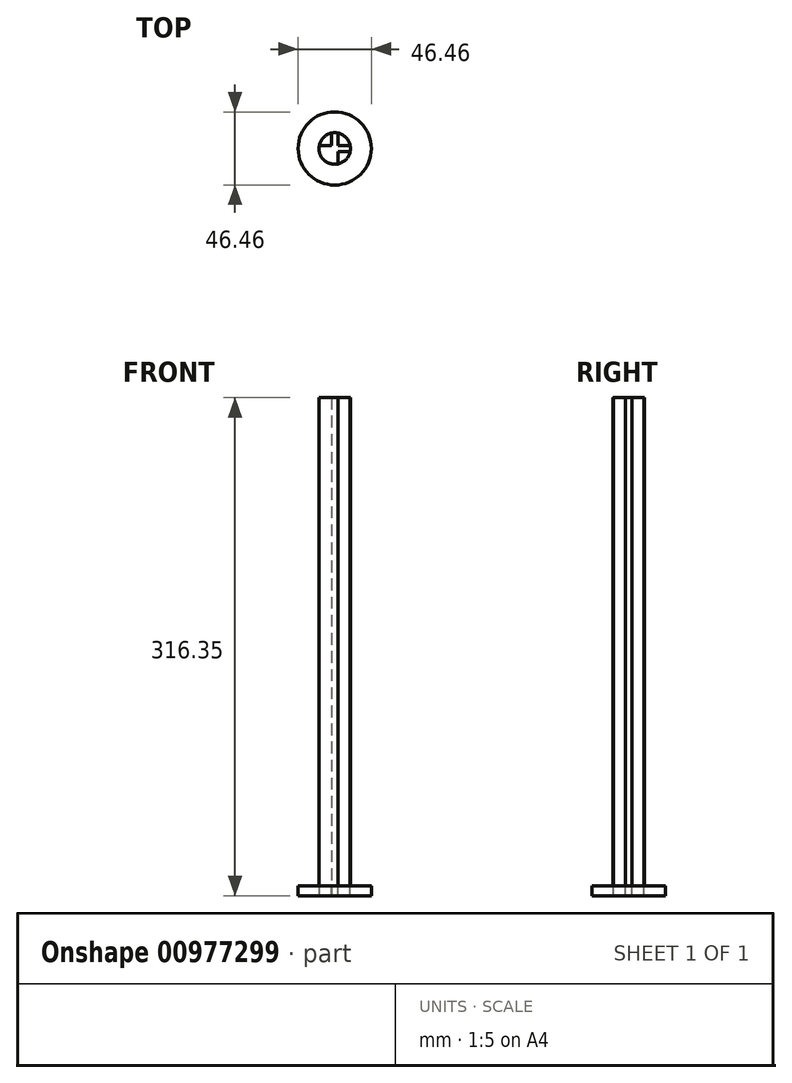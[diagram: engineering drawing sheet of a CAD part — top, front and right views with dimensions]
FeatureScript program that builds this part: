
annotation { "Feature Type Name" : "Feature", "Feature Type Description" : "" }
export const myFeature = defineFeature(function(context is Context, id is Id, definition is map)
    precondition{}
    {
        {
            var Q0;
            Q0=qCreatedBy(makeId("Top.planeOp"),FACE);
            var sketch = newSketch(context, id + "F0", { "sketchPlane" : qUnion([Q0])});
            skPoint(sketch, "E0", {"position": v(0, 0) * mm});
            skCircle(sketch, "E1", {"center": v(0, 0) * mm, "radius": 23.23 * mm});
            skPoint(sketch, "E2", {"position": v(23.64, 0) * mm});
            skLineSegment(sketch, "E3", {"start": v(17.73, 0) * mm, "end": v(23.64, 0) * mm});
            skPoint(sketch, "E4", {"position": v(20.69, 0) * mm});
            skCircle(sketch, "E5.cCircle", {"center": v(0, 0) * mm, "radius": 20.69 * mm, "construction": true});
            skLineSegment(sketch, "E5.0", {"start": v(20.69, 0) * mm, "end": v(10.34, -17.91) * mm});
            skLineSegment(sketch, "E5.1", {"start": v(10.34, -17.91) * mm, "end": v(-10.34, -17.91) * mm});
            skLineSegment(sketch, "E5.2", {"start": v(-10.34, -17.91) * mm, "end": v(-20.69, 0) * mm});
            skLineSegment(sketch, "E5.3", {"start": v(-20.69, 0) * mm, "end": v(-10.34, 17.91) * mm});
            skLineSegment(sketch, "E5.4", {"start": v(-10.34, 17.91) * mm, "end": v(10.34, 17.91) * mm});
            skLineSegment(sketch, "E5.5", {"start": v(10.34, 17.91) * mm, "end": v(20.69, 0) * mm});
            skCircle(sketch, "E6", {"center": v(0, 0) * mm, "radius": 10 * mm});
            skLineSegment(sketch, "E7.bottom", {"start": v(2, 12.5) * mm, "end": v(-2, 12.5) * mm});
            skLineSegment(sketch, "E7.top", {"start": v(2, -12.5) * mm, "end": v(-2, -12.5) * mm});
            skLineSegment(sketch, "E7.left", {"start": v(2, 12.5) * mm, "end": v(2, -12.5) * mm});
            skLineSegment(sketch, "E7.right", {"start": v(-2, 12.5) * mm, "end": v(-2, -12.5) * mm});
            skLineSegment(sketch, "E8.bottom", {"start": v(12.5, 2) * mm, "end": v(-12.5, 2) * mm});
            skLineSegment(sketch, "E8.top", {"start": v(12.5, -2) * mm, "end": v(-12.5, -2) * mm});
            skLineSegment(sketch, "E8.left", {"start": v(12.5, 2) * mm, "end": v(12.5, -2) * mm});
            skLineSegment(sketch, "E8.right", {"start": v(-12.5, 2) * mm, "end": v(-12.5, -2) * mm});
            skLineSegment(sketch, "E9.bottom", {"start": v(2, 8) * mm, "end": v(-2, 8) * mm});
            skLineSegment(sketch, "E9.top", {"start": v(2, -8) * mm, "end": v(-2, -8) * mm});
            skLineSegment(sketch, "E10", {"start": v(-8, 2) * mm, "end": v(-8, -2) * mm});
            skLineSegment(sketch, "E11", {"start": v(8, 2) * mm, "end": v(8, -2) * mm});
            skCircle(sketch, "E12", {"center": v(0, 0) * mm, "radius": 16.33 * mm});
            skSolve(sketch);
        }
        {
            var Q0;
            {var subQ0=sQuery(id+"F0.wireOp",EDGE,"E8.top");var subQ5=sQuery(id+"F0.wireOp",EDGE,"E6");var subQ7=makeQuery(id+"F0.imprint","INTERSECT",VERTEX,{"disambiguationData":[OD(0.0)],"derivedFrom":[subQ5,subQ0]});Q0=makeQuery(id+"F0.imprint","IMPRINT",FACE,{"disambiguationData":[TD([[makeQuery(id+"F0.imprint","IMPRINT",EDGE,{"disambiguationData":[TD([[subQ7,-1.0]])],"derivedFrom":subQ5}),1.0]])]});}
            var Q1;
            {var subQ0=sQuery(id+"F0.wireOp",EDGE,"E7.right");var subQ5=sQuery(id+"F0.wireOp",EDGE,"E6");var subQ6=makeQuery(id+"F0.imprint","INTERSECT",VERTEX,{"disambiguationData":[OD(0.0)],"derivedFrom":[subQ5,subQ0]});Q1=makeQuery(id+"F0.imprint","IMPRINT",FACE,{"disambiguationData":[TD([[makeQuery(id+"F0.imprint","IMPRINT",EDGE,{"disambiguationData":[TD([[subQ6,-1.0]])],"derivedFrom":subQ5}),1.0]])]});}
            var Q2;
            {var subQ0=sQuery(id+"F0.wireOp",EDGE,"E7.left");var subQ4=sQuery(id+"F0.wireOp",EDGE,"E6");var subQ5=makeQuery(id+"F0.imprint","INTERSECT",VERTEX,{"disambiguationData":[OD(0.0)],"derivedFrom":[subQ4,subQ0]});Q2=makeQuery(id+"F0.imprint","IMPRINT",FACE,{"disambiguationData":[TD([[makeQuery(id+"F0.imprint","IMPRINT",EDGE,{"disambiguationData":[TD([[subQ5,1.0]])],"derivedFrom":subQ4}),1.0]])]});}
            var Q3;
            {var subQ2=sQuery(id+"F0.wireOp",EDGE,"E6");var subQ4=sQuery(id+"F0.wireOp",EDGE,"E7.left");var subQ6=makeQuery(id+"F0.imprint","INTERSECT",VERTEX,{"disambiguationData":[OD(1.0)],"derivedFrom":[subQ2,subQ4]});Q3=makeQuery(id+"F0.imprint","IMPRINT",FACE,{"disambiguationData":[TD([[makeQuery(id+"F0.imprint","IMPRINT",EDGE,{"disambiguationData":[TD([[subQ6,-1.0]])],"derivedFrom":subQ2}),1.0]])]});}
            var Q4;
            {var subQ0=sQuery(id+"F0.wireOp",EDGE,"E9.top");Q4=makeQuery(id+"F0.imprint","IMPRINT",FACE,{"disambiguationData":[TD([[makeQuery(id+"F0.imprint","IMPRINT",EDGE,{"derivedFrom":subQ0}),-1.0]])]});}
            var Q5;
            {var subQ5=sQuery(id+"F0.wireOp",EDGE,"E11");Q5=makeQuery(id+"F0.imprint","IMPRINT",FACE,{"disambiguationData":[TD([[makeQuery(id+"F0.imprint","IMPRINT",EDGE,{"derivedFrom":subQ5}),-1.0]])]});}
            var Q6;
            {var subQ0=sQuery(id+"F0.wireOp",EDGE,"E9.bottom");Q6=makeQuery(id+"F0.imprint","IMPRINT",FACE,{"disambiguationData":[TD([[makeQuery(id+"F0.imprint","IMPRINT",EDGE,{"derivedFrom":subQ0}),1.0]])]});}
            var Q7;
            {var subQ5=sQuery(id+"F0.wireOp",EDGE,"E9.bottom");Q7=makeQuery(id+"F0.imprint","IMPRINT",FACE,{"disambiguationData":[TD([[makeQuery(id+"F0.imprint","IMPRINT",EDGE,{"derivedFrom":subQ5}),-1.0]])]});}
            var Q8;
            {var subQ5=sQuery(id+"F0.wireOp",EDGE,"E10");Q8=makeQuery(id+"F0.imprint","IMPRINT",FACE,{"disambiguationData":[TD([[makeQuery(id+"F0.imprint","IMPRINT",EDGE,{"derivedFrom":subQ5}),1.0]])]});}
            var Q9;
            {var subQ5=sQuery(id+"F0.wireOp",EDGE,"E10");Q9=makeQuery(id+"F0.imprint","IMPRINT",FACE,{"disambiguationData":[TD([[makeQuery(id+"F0.imprint","IMPRINT",EDGE,{"derivedFrom":subQ5}),-1.0]])]});}
            var Q10;
            {var subQ0=sQuery(id+"F0.wireOp",EDGE,"E8.bottom");var subQ1=sQuery(id+"F0.wireOp",EDGE,"E7.left");var subQ2=makeQuery(id+"F0.imprint","INTERSECT",VERTEX,{"derivedFrom":[subQ1,subQ0]});Q10=makeQuery(id+"F0.imprint","IMPRINT",FACE,{"disambiguationData":[TD([[makeQuery(id+"F0.imprint","IMPRINT",EDGE,{"disambiguationData":[TD([[subQ2,-1.0]])],"derivedFrom":subQ1}),-1.0]])]});}
            var Q11;
            {var subQ5=sQuery(id+"F0.wireOp",EDGE,"E9.top");Q11=makeQuery(id+"F0.imprint","IMPRINT",FACE,{"disambiguationData":[TD([[makeQuery(id+"F0.imprint","IMPRINT",EDGE,{"derivedFrom":subQ5}),1.0]])]});}
            var Q12;
            {var subQ5=sQuery(id+"F0.wireOp",EDGE,"E11");Q12=makeQuery(id+"F0.imprint","IMPRINT",FACE,{"disambiguationData":[TD([[makeQuery(id+"F0.imprint","IMPRINT",EDGE,{"derivedFrom":subQ5}),1.0]])]});}
            extrude(context, id + "F1", {"entities" : qUnion([Q0, Q1, Q2, Q3, Q4, Q5, Q6, Q7, Q8, Q9, Q10, Q11, Q12]), "depth" : 310 * mm, "offsetDistance" : 25.4 * mm});
        }
        {
            var Q0;
            {var subQ2=sQuery(id+"F0.wireOp",EDGE,"E6");var subQ4=sQuery(id+"F0.wireOp",EDGE,"E7.left");var subQ6=makeQuery(id+"F0.imprint","INTERSECT",VERTEX,{"disambiguationData":[OD(1.0)],"derivedFrom":[subQ2,subQ4]});Q0=makeQuery(id+"F0.imprint","IMPRINT",FACE,{"disambiguationData":[TD([[makeQuery(id+"F0.imprint","IMPRINT",EDGE,{"disambiguationData":[TD([[subQ6,-1.0]])],"derivedFrom":subQ2}),1.0]])]});}
            var Q1;
            {var subQ0=sQuery(id+"F0.wireOp",EDGE,"E7.left");var subQ4=sQuery(id+"F0.wireOp",EDGE,"E6");var subQ5=makeQuery(id+"F0.imprint","INTERSECT",VERTEX,{"disambiguationData":[OD(0.0)],"derivedFrom":[subQ4,subQ0]});Q1=makeQuery(id+"F0.imprint","IMPRINT",FACE,{"disambiguationData":[TD([[makeQuery(id+"F0.imprint","IMPRINT",EDGE,{"disambiguationData":[TD([[subQ5,1.0]])],"derivedFrom":subQ4}),1.0]])]});}
            var Q2;
            {var subQ5=sQuery(id+"F0.wireOp",EDGE,"E8.left");Q2=makeQuery(id+"F0.imprint","IMPRINT",FACE,{"disambiguationData":[TD([[makeQuery(id+"F0.imprint","IMPRINT",EDGE,{"derivedFrom":subQ5}),-1.0]])]});}
            var Q3;
            {var subQ5=sQuery(id+"F0.wireOp",EDGE,"E11");Q3=makeQuery(id+"F0.imprint","IMPRINT",FACE,{"disambiguationData":[TD([[makeQuery(id+"F0.imprint","IMPRINT",EDGE,{"derivedFrom":subQ5}),1.0]])]});}
            var Q4;
            Q4=makeQuery(id+"F0.imprint","IMPRINT",FACE,{"disambiguationData":[TD([[makeQuery(id+"F0.imprint","IMPRINT",EDGE,{"derivedFrom":sQuery(id+"F0.wireOp",EDGE,"E1")}),1.0]])]});
            var Q5;
            {var subQ10=sQuery(id+"F0.wireOp",EDGE,"E7.bottom");Q5=makeQuery(id+"F0.imprint","IMPRINT",FACE,{"disambiguationData":[TD([[makeQuery(id+"F0.imprint","IMPRINT",EDGE,{"derivedFrom":subQ10}),-1.0]])]});}
            var Q6;
            Q6=makeQuery(id+"F0.imprint","IMPRINT",FACE,{"disambiguationData":[TD([[makeQuery(id+"F0.imprint","IMPRINT",EDGE,{"derivedFrom":sQuery(id+"F0.wireOp",EDGE,"E5.0")}),-1.0]])]});
            var Q7;
            {var subQ5=sQuery(id+"F0.wireOp",EDGE,"E7.bottom");Q7=makeQuery(id+"F0.imprint","IMPRINT",FACE,{"disambiguationData":[TD([[makeQuery(id+"F0.imprint","IMPRINT",EDGE,{"derivedFrom":subQ5}),1.0]])]});}
            var Q8;
            {var subQ5=sQuery(id+"F0.wireOp",EDGE,"E8.right");Q8=makeQuery(id+"F0.imprint","IMPRINT",FACE,{"disambiguationData":[TD([[makeQuery(id+"F0.imprint","IMPRINT",EDGE,{"derivedFrom":subQ5}),1.0]])]});}
            var Q9;
            {var subQ5=sQuery(id+"F0.wireOp",EDGE,"E7.top");Q9=makeQuery(id+"F0.imprint","IMPRINT",FACE,{"disambiguationData":[TD([[makeQuery(id+"F0.imprint","IMPRINT",EDGE,{"derivedFrom":subQ5}),-1.0]])]});}
            var Q10;
            {var subQ0=sQuery(id+"F0.wireOp",EDGE,"E9.top");Q10=makeQuery(id+"F0.imprint","IMPRINT",FACE,{"disambiguationData":[TD([[makeQuery(id+"F0.imprint","IMPRINT",EDGE,{"derivedFrom":subQ0}),-1.0]])]});}
            var Q11;
            {var subQ0=sQuery(id+"F0.wireOp",EDGE,"E9.bottom");Q11=makeQuery(id+"F0.imprint","IMPRINT",FACE,{"disambiguationData":[TD([[makeQuery(id+"F0.imprint","IMPRINT",EDGE,{"derivedFrom":subQ0}),1.0]])]});}
            var Q12;
            {var subQ5=sQuery(id+"F0.wireOp",EDGE,"E11");Q12=makeQuery(id+"F0.imprint","IMPRINT",FACE,{"disambiguationData":[TD([[makeQuery(id+"F0.imprint","IMPRINT",EDGE,{"derivedFrom":subQ5}),-1.0]])]});}
            var Q13;
            {var subQ0=sQuery(id+"F0.wireOp",EDGE,"E7.right");var subQ5=sQuery(id+"F0.wireOp",EDGE,"E6");var subQ6=makeQuery(id+"F0.imprint","INTERSECT",VERTEX,{"disambiguationData":[OD(0.0)],"derivedFrom":[subQ5,subQ0]});Q13=makeQuery(id+"F0.imprint","IMPRINT",FACE,{"disambiguationData":[TD([[makeQuery(id+"F0.imprint","IMPRINT",EDGE,{"disambiguationData":[TD([[subQ6,-1.0]])],"derivedFrom":subQ5}),1.0]])]});}
            var Q14;
            {var subQ0=sQuery(id+"F0.wireOp",EDGE,"E8.top");var subQ5=sQuery(id+"F0.wireOp",EDGE,"E6");var subQ7=makeQuery(id+"F0.imprint","INTERSECT",VERTEX,{"disambiguationData":[OD(0.0)],"derivedFrom":[subQ5,subQ0]});Q14=makeQuery(id+"F0.imprint","IMPRINT",FACE,{"disambiguationData":[TD([[makeQuery(id+"F0.imprint","IMPRINT",EDGE,{"disambiguationData":[TD([[subQ7,-1.0]])],"derivedFrom":subQ5}),1.0]])]});}
            var Q15;
            Q15=makeQuery(id+"F1.opExtrude","CAP_FACE",FACE,{"disambiguationData":[OSD([sQuery(id+"F0.wireOp",EDGE,"E6")])],"isStart":true});
            var Q16;
            {var subQ5=sQuery(id+"F0.wireOp",EDGE,"E9.top");Q16=makeQuery(id+"F0.imprint","IMPRINT",FACE,{"disambiguationData":[TD([[makeQuery(id+"F0.imprint","IMPRINT",EDGE,{"derivedFrom":subQ5}),1.0]])]});}
            var Q17;
            {var subQ5=sQuery(id+"F0.wireOp",EDGE,"E9.bottom");Q17=makeQuery(id+"F0.imprint","IMPRINT",FACE,{"disambiguationData":[TD([[makeQuery(id+"F0.imprint","IMPRINT",EDGE,{"derivedFrom":subQ5}),-1.0]])]});}
            var Q18;
            {var subQ0=sQuery(id+"F0.wireOp",EDGE,"E8.bottom");var subQ1=sQuery(id+"F0.wireOp",EDGE,"E7.left");var subQ2=makeQuery(id+"F0.imprint","INTERSECT",VERTEX,{"derivedFrom":[subQ1,subQ0]});Q18=makeQuery(id+"F0.imprint","IMPRINT",FACE,{"disambiguationData":[TD([[makeQuery(id+"F0.imprint","IMPRINT",EDGE,{"disambiguationData":[TD([[subQ2,-1.0]])],"derivedFrom":subQ1}),-1.0]])]});}
            var Q19;
            {var subQ5=sQuery(id+"F0.wireOp",EDGE,"E10");Q19=makeQuery(id+"F0.imprint","IMPRINT",FACE,{"disambiguationData":[TD([[makeQuery(id+"F0.imprint","IMPRINT",EDGE,{"derivedFrom":subQ5}),1.0]])]});}
            var Q20;
            {var subQ5=sQuery(id+"F0.wireOp",EDGE,"E10");Q20=makeQuery(id+"F0.imprint","IMPRINT",FACE,{"disambiguationData":[TD([[makeQuery(id+"F0.imprint","IMPRINT",EDGE,{"derivedFrom":subQ5}),-1.0]])]});}
            extrude(context, id + "F2", {"entities" : qUnion([Q0, Q1, Q2, Q3, Q4, Q5, Q6, Q7, Q8, Q9, Q10, Q11, Q12, Q13, Q14, Q15, Q16, Q17, Q18, Q19, Q20]), "operationType" : NewBodyOperationType.ADD, "oppositeDirection" : true, "depth" : 6.35 * mm, "offsetDistance" : 25.4 * mm});
        }
    });
